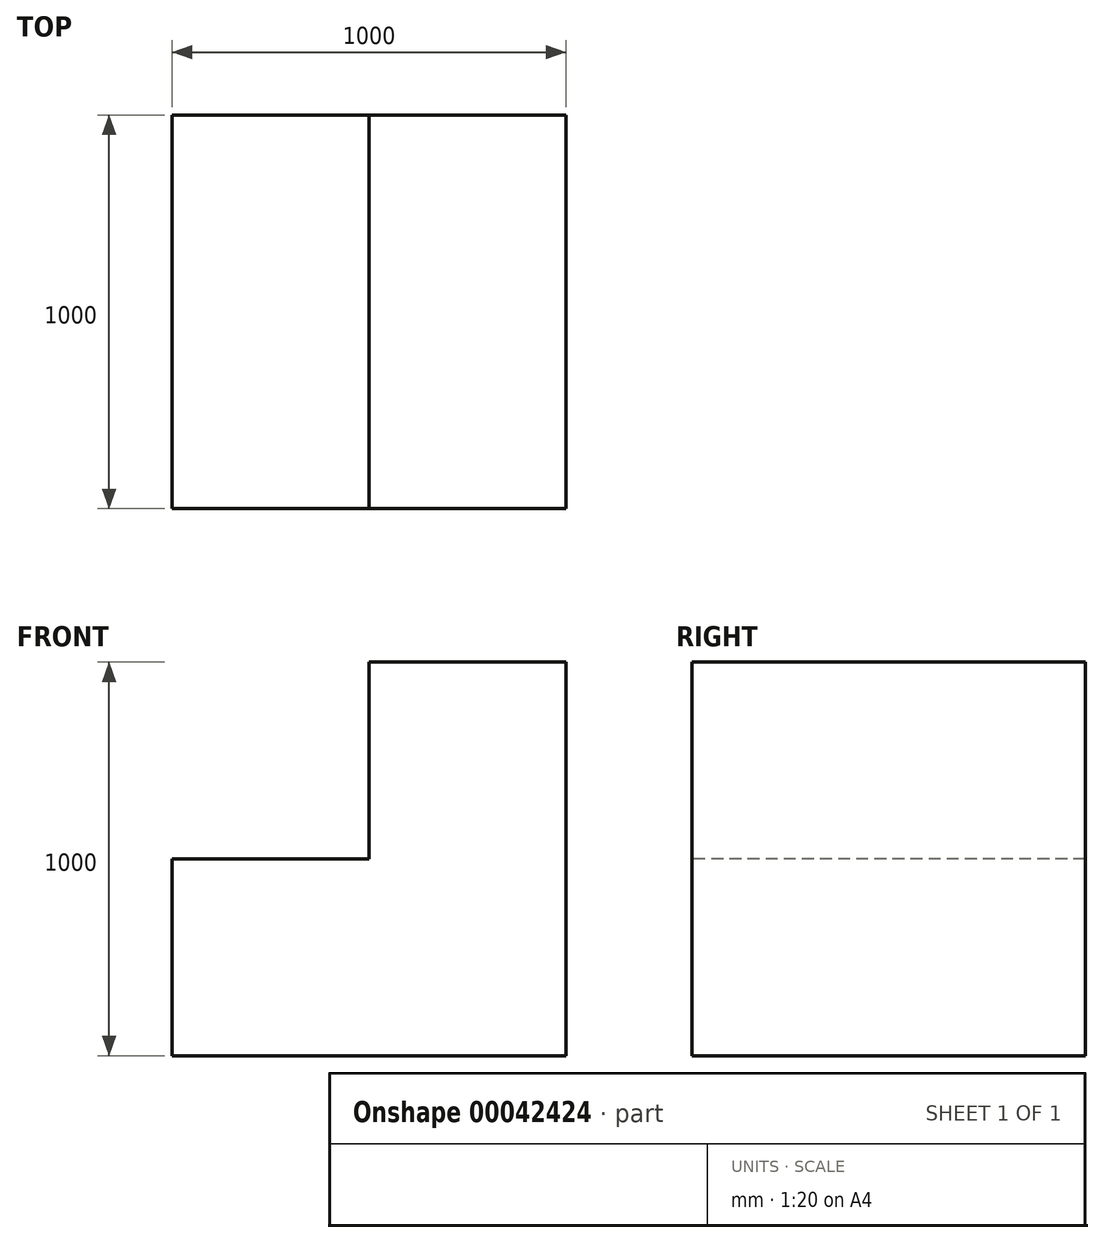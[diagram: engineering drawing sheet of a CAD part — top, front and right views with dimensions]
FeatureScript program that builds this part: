
annotation { "Feature Type Name" : "Feature", "Feature Type Description" : "" }
export const myFeature = defineFeature(function(context is Context, id is Id, definition is map)
    precondition{}
    {
        {
            var Q0;
            Q0=qCreatedBy(makeId("Top.planeOp"),FACE);
            var sketch = newSketch(context, id + "F0", { "sketchPlane" : qUnion([Q0])});
            skLineSegment(sketch, "E0.bottom", {"start": v(-500, 500) * mm, "end": v(500, 500) * mm});
            skLineSegment(sketch, "E0.top", {"start": v(-500, -500) * mm, "end": v(500, -500) * mm});
            skLineSegment(sketch, "E0.left", {"start": v(-500, 500) * mm, "end": v(-500, -500) * mm});
            skLineSegment(sketch, "E0.right", {"start": v(500, 500) * mm, "end": v(500, -500) * mm});
            skLineSegment(sketch, "E1", {"start": v(-500, 500) * mm, "end": v(500, -500) * mm, "construction": true});
            skLineSegment(sketch, "E2", {"start": v(500, 500) * mm, "end": v(-500, -500) * mm, "construction": true});
            skPoint(sketch, "E3", {"position": v(0, 0) * mm});
            skSolve(sketch);
        }
        {
            var Q0;
            Q0=makeQuery(id+"F0.imprint","IMPRINT",FACE,{"disambiguationData":[TD([[makeQuery(id+"F0.imprint","IMPRINT",EDGE,{"derivedFrom":sQuery(id+"F0.wireOp",EDGE,"E0.bottom")}),-1.0]])]});
            extrude(context, id + "F1", {"entities" : qUnion([Q0]), "depth" : 1000 * mm});
        }
        {
            var Q0;
            Q0=makeQuery(id+"F1.opExtrude","CAP_FACE",FACE,{"disambiguationData":[OSD([sQuery(id+"F0.wireOp",EDGE,"E0.bottom"),sQuery(id+"F0.wireOp",EDGE,"E0.top"),sQuery(id+"F0.wireOp",EDGE,"E0.left"),sQuery(id+"F0.wireOp",EDGE,"E0.right")])],"isStart":false});
            var sketch = newSketch(context, id + "F2", { "sketchPlane" : qUnion([Q0])});
            skLineSegment(sketch, "E4.bottom", {"start": v(-500, 500) * mm, "end": v(0, 500) * mm});
            skLineSegment(sketch, "E4.top", {"start": v(-500, -500) * mm, "end": v(0, -500) * mm});
            skLineSegment(sketch, "E4.left", {"start": v(-500, 500) * mm, "end": v(-500, -500) * mm});
            skLineSegment(sketch, "E4.right", {"start": v(0, 500) * mm, "end": v(0, -500) * mm});
            skSolve(sketch);
        }
        {
            var Q0;
            Q0=makeQuery(id+"F2.imprint","IMPRINT",FACE,{"disambiguationData":[TD([[makeQuery(id+"F2.imprint","IMPRINT",EDGE,{"derivedFrom":sQuery(id+"F2.wireOp",EDGE,"E4.bottom")}),-1.0]])]});
            extrude(context, id + "F3", {"entities" : qUnion([Q0]), "operationType" : NewBodyOperationType.REMOVE, "oppositeDirection" : true, "depth" : 500 * mm});
        }
    });
